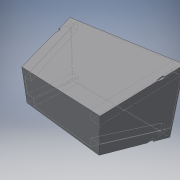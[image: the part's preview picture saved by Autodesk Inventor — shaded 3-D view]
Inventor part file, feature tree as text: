
AUTODESK INVENTOR PART (.ipt)
format: ipt  version: 2019 (Build 230136000, 136)  size: 162,816 bytes
history: native  units: in
note: dims shown in document units (in); Inventor stores cm internally (conversion verified against a paired STEP export)
features: sketch x5, plane x2, loft x2, extrude x1
ambient origin geometry x8: Origin, YZ Plane, XZ Plane, XY Plane, X Axis, Y Axis, Z Axis, Center Point
bodies: Solid1 (feature_tree)
feature tree (10):
  sketch  "Sketch1"  dims[d0=14.125in d1=8.25in]
  plane  "Work Plane1"
  loft  "Loft1"
  sketch  "Sketch3"  dims[d4=2.0in d5=0.0in d6=90.0deg]
  plane  "Work Plane2"
  loft  "Loft2"
  extrude  "Extrusion1"  TaperAngle=0.0deg  [1 undecoded]
  sketch  "Sketch2"  dims[d2=8.0in d3=2.0in]
  sketch  "Sketch5"  dims[d7=0.0in d8=90.0deg]
  sketch  "Sketch6"  dims[d9=0.125in d10=0.125in d11=1.0in d12=7.875in d15=0.125in d16=0.0in d17=90.0deg d18=0.0in d19=90.0deg d20=0.5in d21=0.5in d22=0.25in d23=1.0in d24=0.0in]
note: 1 required parameter value undecoded (feature->parameter linkage not recoverable at this tier; creation-order binding heuristic only, values carry confidence <= 0.55)
